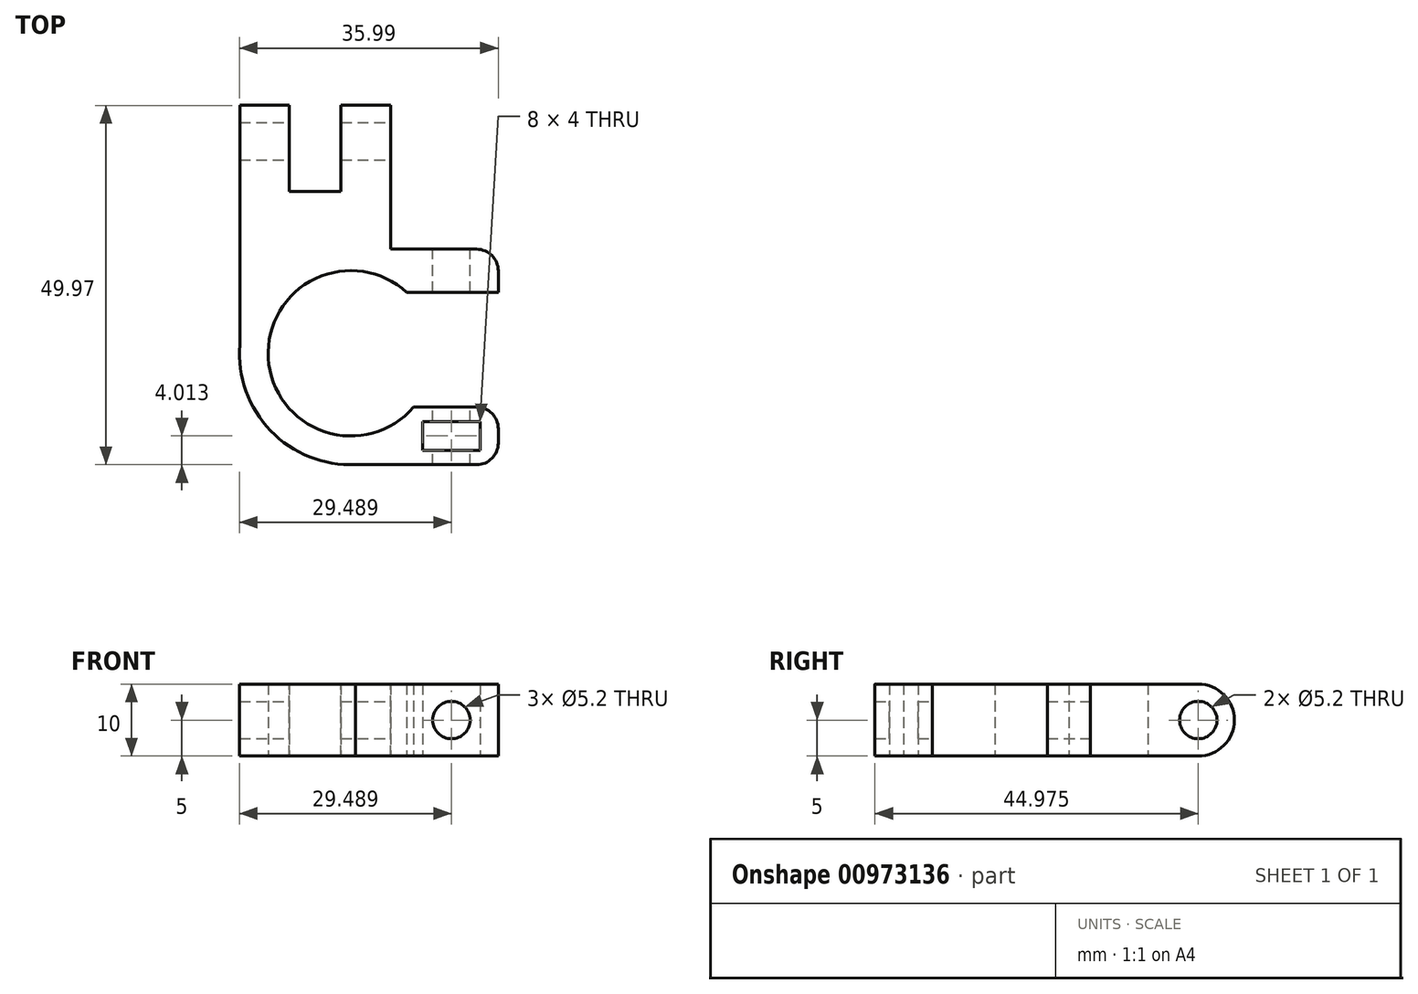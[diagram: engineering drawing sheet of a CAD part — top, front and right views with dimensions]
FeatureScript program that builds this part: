
annotation { "Feature Type Name" : "Feature", "Feature Type Description" : "" }
export const myFeature = defineFeature(function(context is Context, id is Id, definition is map)
    precondition{}
    {
        {
            var Q0;
            Q0=qCreatedBy(makeId("Top.planeOp"),FACE);
            var sketch = newSketch(context, id + "F0", { "sketchPlane" : qUnion([Q0])});
            skLineSegment(sketch, "E0", {"start": v(5.54, 14.47) * mm, "end": v(5.54, 14.47) * mm});
            skLineSegment(sketch, "E1.rect.top", {"start": v(20.49, 14.47) * mm, "end": v(5.54, 14.47) * mm});
            skLineSegment(sketch, "E1.rect.left", {"start": v(20.49, -15.49) * mm, "end": v(20.49, -7.49) * mm});
            skLineSegment(sketch, "E2.0", {"start": v(20.49, 8.47) * mm, "end": v(7.77, 8.47) * mm});
            skLineSegment(sketch, "E3.0", {"start": v(20.49, -7.49) * mm, "end": v(8.73, -7.49) * mm});
            skLineSegment(sketch, "E4.trimOffspring", {"start": v(20.49, 8.47) * mm, "end": v(20.49, 14.47) * mm});
            skCircle(sketch, "E5.converted", {"center": v(0, 0) * mm, "radius": 11.5 * mm, "construction": true});
            skArc(sketch, "E6.0", {"start": v(7.77, 8.47) * mm, "mid": v(-11.48, -0.69) * mm, "end": v(8.73, -7.49) * mm});
            skLineSegment(sketch, "E7.rect.bottom", {"start": v(-15.46, 34.47) * mm, "end": v(-8.56, 34.47) * mm});
            skLineSegment(sketch, "E7.rect.left", {"start": v(-15.46, 34.47) * mm, "end": v(-15.46, 1.16) * mm});
            skLineSegment(sketch, "E7.rect.right", {"start": v(5.54, 34.47) * mm, "end": v(5.54, 14.47) * mm});
            skPoint(sketch, "E7.rect.middle", {"position": v(0.06, 0.12) * mm});
            skLineSegment(sketch, "E8.0", {"start": v(-8.56, 22.47) * mm, "end": v(-1.36, 22.47) * mm});
            skLineSegment(sketch, "E9.0", {"start": v(-8.56, 34.47) * mm, "end": v(-8.56, 22.47) * mm});
            skLineSegment(sketch, "E10.0", {"start": v(-1.36, 34.47) * mm, "end": v(-1.36, 22.47) * mm});
            skArc(sketch, "E11.trimOffspring", {"start": v(-15.46, 1.16) * mm, "mid": v(-11.15, -10.77) * mm, "end": v(0.62, -15.49) * mm});
            skLineSegment(sketch, "E12.trimOffspring", {"start": v(-1.36, 34.47) * mm, "end": v(5.54, 34.47) * mm});
            skLineSegment(sketch, "E13.0", {"start": v(20.49, -15.49) * mm, "end": v(11.59, -15.49) * mm});
            skLineSegment(sketch, "E14", {"start": v(11.59, -15.49) * mm, "end": v(0.62, -15.49) * mm});
            skLineSegment(sketch, "E15.0", {"start": v(17.99, -13.49) * mm, "end": v(17.99, -9.49) * mm});
            skLineSegment(sketch, "E16.0", {"start": v(9.99, -13.49) * mm, "end": v(9.99, -9.49) * mm});
            skLineSegment(sketch, "E17", {"start": v(20.49, -7.49) * mm, "end": v(20.49, 8.47) * mm, "construction": true});
            skLineSegment(sketch, "E18.0", {"start": v(17.99, -13.49) * mm, "end": v(9.99, -13.49) * mm});
            skLineSegment(sketch, "E19.0", {"start": v(17.99, -9.49) * mm, "end": v(9.99, -9.49) * mm});
            skLineSegment(sketch, "E20", {"start": v(20.49, 0.5) * mm, "end": v(11.49, 0.5) * mm, "construction": true});
            skSolve(sketch);
        }
        {
            var Q0;
            Q0=qSketchRegion(id+"F0",true);
            extrude(context, id + "F1", {"entities" : qUnion([Q0]), "depth" : 10 * mm});
        }
        {
            var Q0;
            Q0=makeQuery(id+"F1.opExtrude","SWEPT_FACE",FACE,{"disambiguationData":[OSD([sQuery(id+"F0.wireOp",EDGE,"E7.rect.right")])]});
            var sketch = newSketch(context, id + "F2", { "sketchPlane" : qUnion([Q0])});
            skLineSegment(sketch, "E21.0.0", {"start": v(29.47, 0) * mm, "end": v(34.47, 0) * mm});
            skLineSegment(sketch, "E21.0.1", {"start": v(34.47, 0) * mm, "end": v(34.47, 10) * mm});
            skLineSegment(sketch, "E21.0.2", {"start": v(34.47, 10) * mm, "end": v(29.47, 10) * mm});
            skCircle(sketch, "E22", {"center": v(29.47, 5) * mm, "radius": 2.6 * mm});
            skPoint(sketch, "E22.centerSnap0", {"position": v(29.47, 10) * mm});
            skArc(sketch, "E23", {"start": v(29.47, 0) * mm, "mid": v(34.47, 5) * mm, "end": v(29.47, 10) * mm});
            skSolve(sketch);
        }
        {
            var Q0;
            Q0=qSketchRegion(id+"F2",true);
            var Q1;
            Q1=makeQuery(id+"F1.opExtrude","SWEPT_FACE",FACE,{"disambiguationData":[OSD([sQuery(id+"F0.wireOp",EDGE,"E7.rect.left")])]});
            extrude(context, id + "F3", {"entities" : qUnion([Q0]), "operationType" : NewBodyOperationType.REMOVE, "endBound" : BoundingType.UP_TO_SURFACE, "oppositeDirection" : true, "endBoundEntityFace" : qUnion([Q1]), "depth" : 25 * mm});
        }
        {
            var Q0;
            Q0=makeQuery(id+"F1.opExtrude","SWEPT_FACE",FACE,{"disambiguationData":[OSD([sQuery(id+"F0.wireOp",EDGE,"E18.0")])]});
            var sketch = newSketch(context, id + "F4", { "sketchPlane" : qUnion([Q0])});
            skLineSegment(sketch, "E24.0.0", {"start": v(-17.99, 0) * mm, "end": v(-9.99, 0) * mm, "construction": true});
            skLineSegment(sketch, "E24.0.1", {"start": v(-9.99, 0) * mm, "end": v(-9.99, 10) * mm, "construction": true});
            skLineSegment(sketch, "E24.0.2", {"start": v(-9.99, 10) * mm, "end": v(-17.99, 10) * mm, "construction": true});
            skLineSegment(sketch, "E24.0.3", {"start": v(-17.99, 10) * mm, "end": v(-17.99, 0) * mm, "construction": true});
            skCircle(sketch, "E25", {"center": v(-13.99, 5) * mm, "radius": 2.6 * mm});
            skPoint(sketch, "E25.centerSnap0", {"position": v(-9.99, 5) * mm});
            skPoint(sketch, "E25.centerSnap1", {"position": v(-13.99, 10) * mm});
            skSolve(sketch);
        }
        {
            var Q0;
            Q0=qSketchRegion(id+"F4",true);
            extrude(context, id + "F5", {"entities" : qUnion([Q0]), "operationType" : NewBodyOperationType.REMOVE, "endBound" : BoundingType.SYMMETRIC, "oppositeDirection" : true, "depth" : 100 * mm});
        }
        {
            var Q0;
            Q0=makeQuery(id+"F1.opExtrude","SWEPT_EDGE",EDGE,{"disambiguationData":[OSD([sQuery(id+"F0.wireOp",EDGE,"E1.rect.top"),sQuery(id+"F0.wireOp",EDGE,"E4.trimOffspring")])]});
            var Q1;
            Q1=makeQuery(id+"F1.opExtrude","SWEPT_EDGE",EDGE,{"disambiguationData":[OSD([sQuery(id+"F0.wireOp",EDGE,"E1.rect.left"),sQuery(id+"F0.wireOp",EDGE,"E3.0")])]});
            var Q2;
            Q2=makeQuery(id+"F1.opExtrude","SWEPT_EDGE",EDGE,{"disambiguationData":[OSD([sQuery(id+"F0.wireOp",EDGE,"E1.rect.left"),sQuery(id+"F0.wireOp",EDGE,"E13.0")])]});
            fillet(context, id + "F6", {"entities" : qUnion([Q0, Q1, Q2]), "radius" : 3 * mm, "tangentPropagation" : true, "allowEdgeOverflow" : false});
        }
    });
